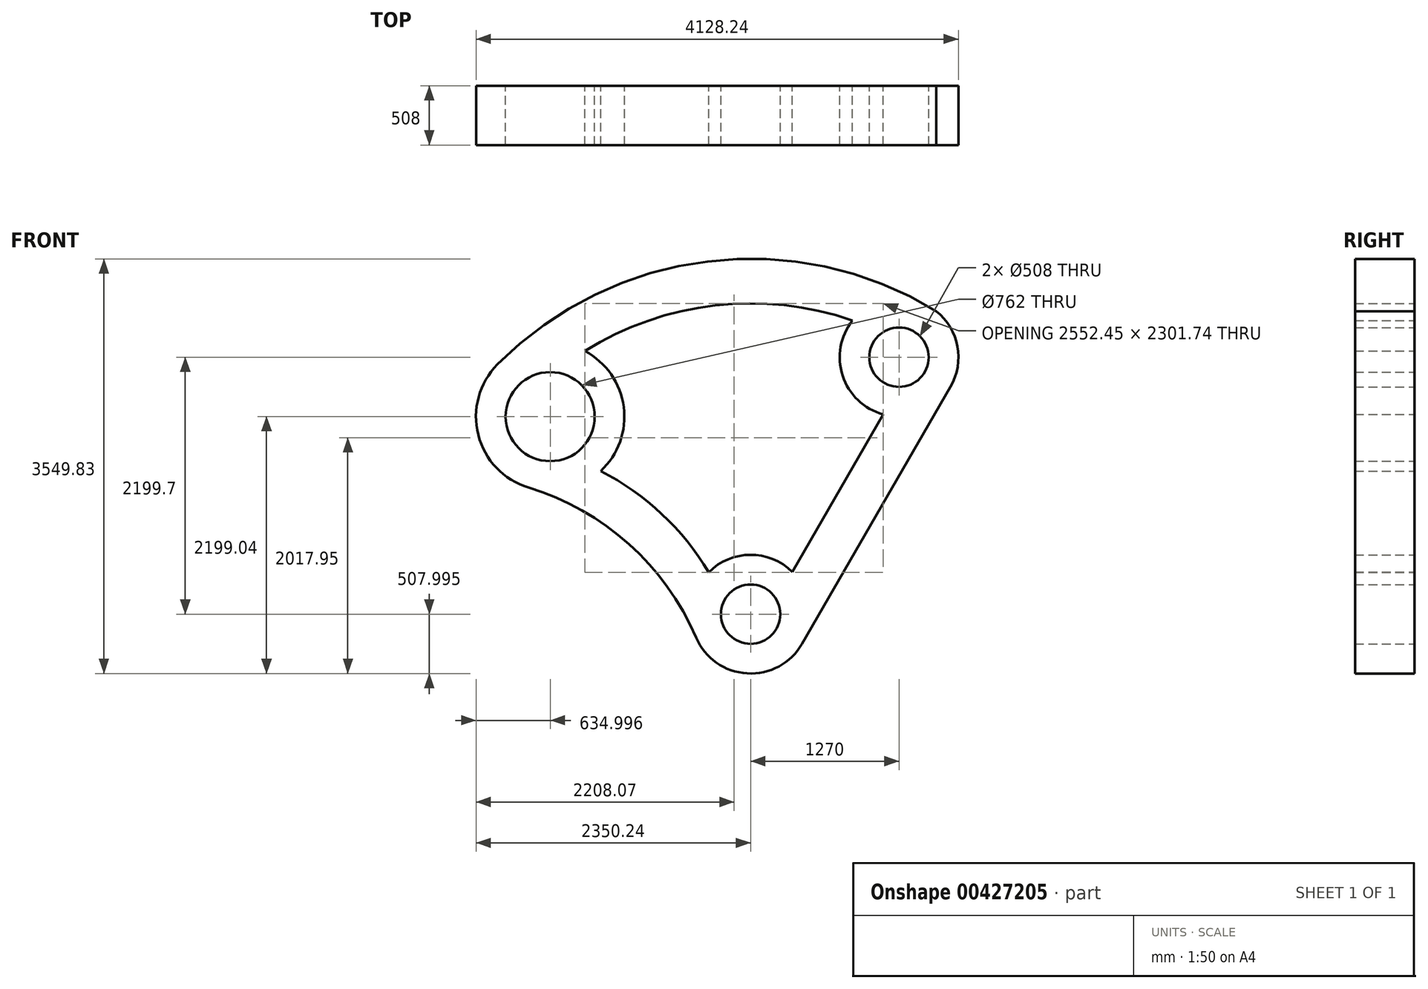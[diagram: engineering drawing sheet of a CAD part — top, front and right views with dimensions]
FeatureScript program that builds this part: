
annotation { "Feature Type Name" : "Feature", "Feature Type Description" : "" }
export const myFeature = defineFeature(function(context is Context, id is Id, definition is map)
    precondition{}
    {
        {
            var Q0;
            Q0=qCreatedBy(makeId("Front.planeOp"),FACE);
            var sketch = newSketch(context, id + "F0", { "sketchPlane" : qUnion([Q0])});
            skArc(sketch, "E0", {"start": v(871.3, 2520.66) * mm, "mid": v(787.12, 2048.1) * mm, "end": v(1134.05, 1716.4) * mm});
            skArc(sketch, "E1", {"start": v(355.92, 368.64) * mm, "mid": v(-2.4, 514.16) * mm, "end": v(-359.33, 365.26) * mm});
            skArc(sketch, "E2", {"start": v(-1283.17, 1231.87) * mm, "mid": v(-1085.68, 1780.13) * mm, "end": v(-1418.4, 2258.55) * mm});
            skArc(sketch, "E3", {"start": v(1589.94, 2600.46) * mm, "mid": v(-367.78, 3025.73) * mm, "end": v(-2166.62, 2143.84) * mm});
            skLineSegment(sketch, "E4", {"start": v(1709.94, 1951.87) * mm, "end": v(439.94, -247.83) * mm});
            skLineSegment(sketch, "E5.trimOffspring", {"start": v(0, 6.17) * mm, "end": v(0, 0) * mm});
            skPoint(sketch, "E6.start.orphan", {"position": v(0, 3348.8) * mm});
            skArc(sketch, "E7", {"start": v(-466.74, -194.38) * mm, "mid": v(-1041.84, 605.96) * mm, "end": v(-1900.42, 1089.8) * mm});
            skCircle(sketch, "E8", {"center": v(-1715.24, 1697.2) * mm, "radius": 381 * mm});
            skCircle(sketch, "E9", {"center": v(1270, 2205.87) * mm, "radius": 254 * mm});
            skCircle(sketch, "E10", {"center": v(0, 6.17) * mm, "radius": 254 * mm});
            skArc(sketch, "E11.trimOffspring", {"start": v(871.3, 2520.66) * mm, "mid": v(-303.33, 2649.7) * mm, "end": v(-1418.4, 2258.55) * mm});
            skLineSegment(sketch, "E12", {"start": v(1134.05, 1716.4) * mm, "end": v(355.92, 368.64) * mm});
            skArc(sketch, "E13.trimOffspring", {"start": v(-359.33, 365.26) * mm, "mid": v(-760.03, 863.83) * mm, "end": v(-1283.17, 1231.87) * mm});
            skArc(sketch, "E14.trimOffspring", {"start": v(-2166.62, 2143.84) * mm, "mid": v(-2330.91, 1541.72) * mm, "end": v(-1900.42, 1089.8) * mm});
            skArc(sketch, "E15.trimOffspring", {"start": v(1709.94, 1951.87) * mm, "mid": v(1748.6, 2376.17) * mm, "end": v(1450.6, 2680.68) * mm});
            skArc(sketch, "E16.trimOffspring", {"start": v(-466.74, -194.38) * mm, "mid": v(-29.9, -500.95) * mm, "end": v(439.94, -247.83) * mm});
            skSolve(sketch);
        }
        {
            var Q0;
            Q0=makeQuery(id+"F0.imprint","IMPRINT",FACE,{"disambiguationData":[TD([[makeQuery(id+"F0.imprint","IMPRINT",EDGE,{"derivedFrom":sQuery(id+"F0.wireOp",EDGE,"E0")}),1.0]])]});
            extrude(context, id + "F1", {"entities" : qUnion([Q0]), "depth" : 508 * mm});
        }
    });
